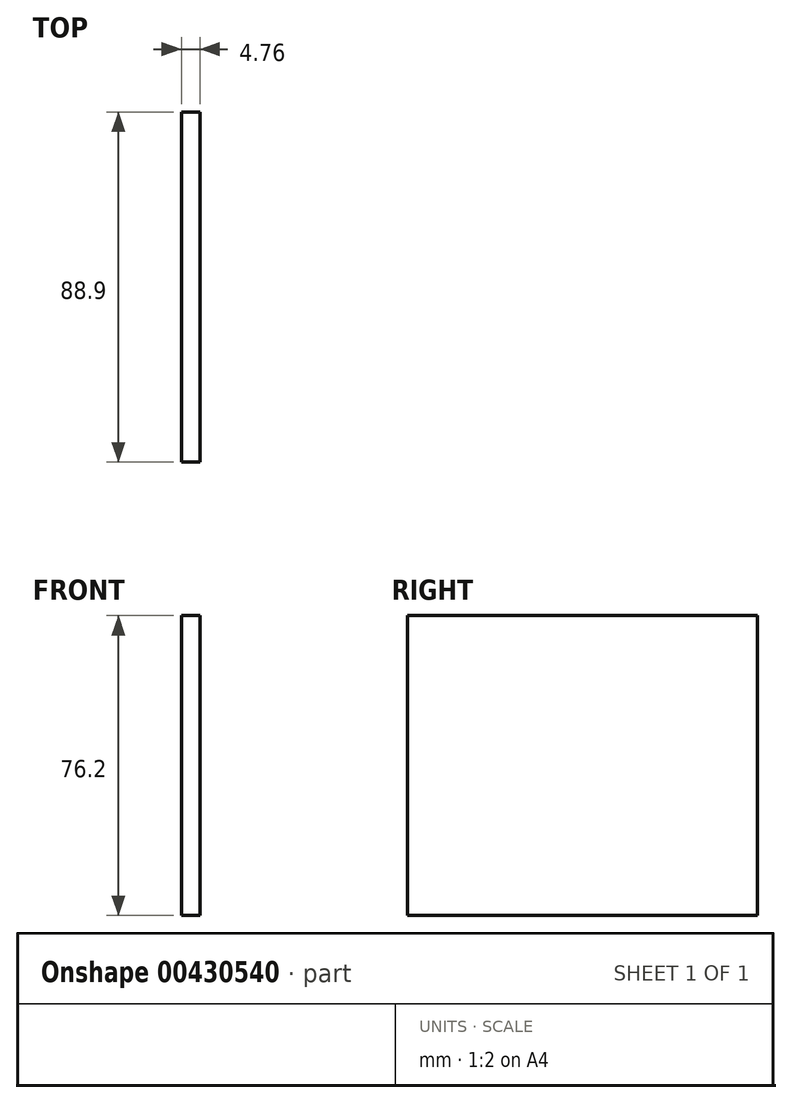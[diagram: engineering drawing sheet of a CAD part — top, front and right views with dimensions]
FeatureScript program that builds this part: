
annotation { "Feature Type Name" : "Feature", "Feature Type Description" : "" }
export const myFeature = defineFeature(function(context is Context, id is Id, definition is map)
    precondition{}
    {
        {
            var Q0;
            Q0=qCreatedBy(makeId("Right.planeOp"),FACE);
            var sketch = newSketch(context, id + "F0", { "sketchPlane" : qUnion([Q0])});
            skLineSegment(sketch, "E0.bottom", {"start": v(-46.54, 38.67) * mm, "end": v(42.36, 38.67) * mm});
            skLineSegment(sketch, "E0.top", {"start": v(-46.54, -37.53) * mm, "end": v(42.36, -37.53) * mm});
            skLineSegment(sketch, "E0.left", {"start": v(-46.54, 38.67) * mm, "end": v(-46.54, -37.53) * mm});
            skLineSegment(sketch, "E0.right", {"start": v(42.36, 38.67) * mm, "end": v(42.36, -37.53) * mm});
            skSolve(sketch);
        }
        {
            var Q0;
            Q0=makeQuery(id+"F0.imprint","IMPRINT",FACE,{"disambiguationData":[TD([[makeQuery(id+"F0.imprint","IMPRINT",EDGE,{"derivedFrom":sQuery(id+"F0.wireOp",EDGE,"E0.bottom")}),-1.0]])]});
            extrude(context, id + "F1", {"entities" : qUnion([Q0]), "depth" : 4.76 * mm});
        }
    });
